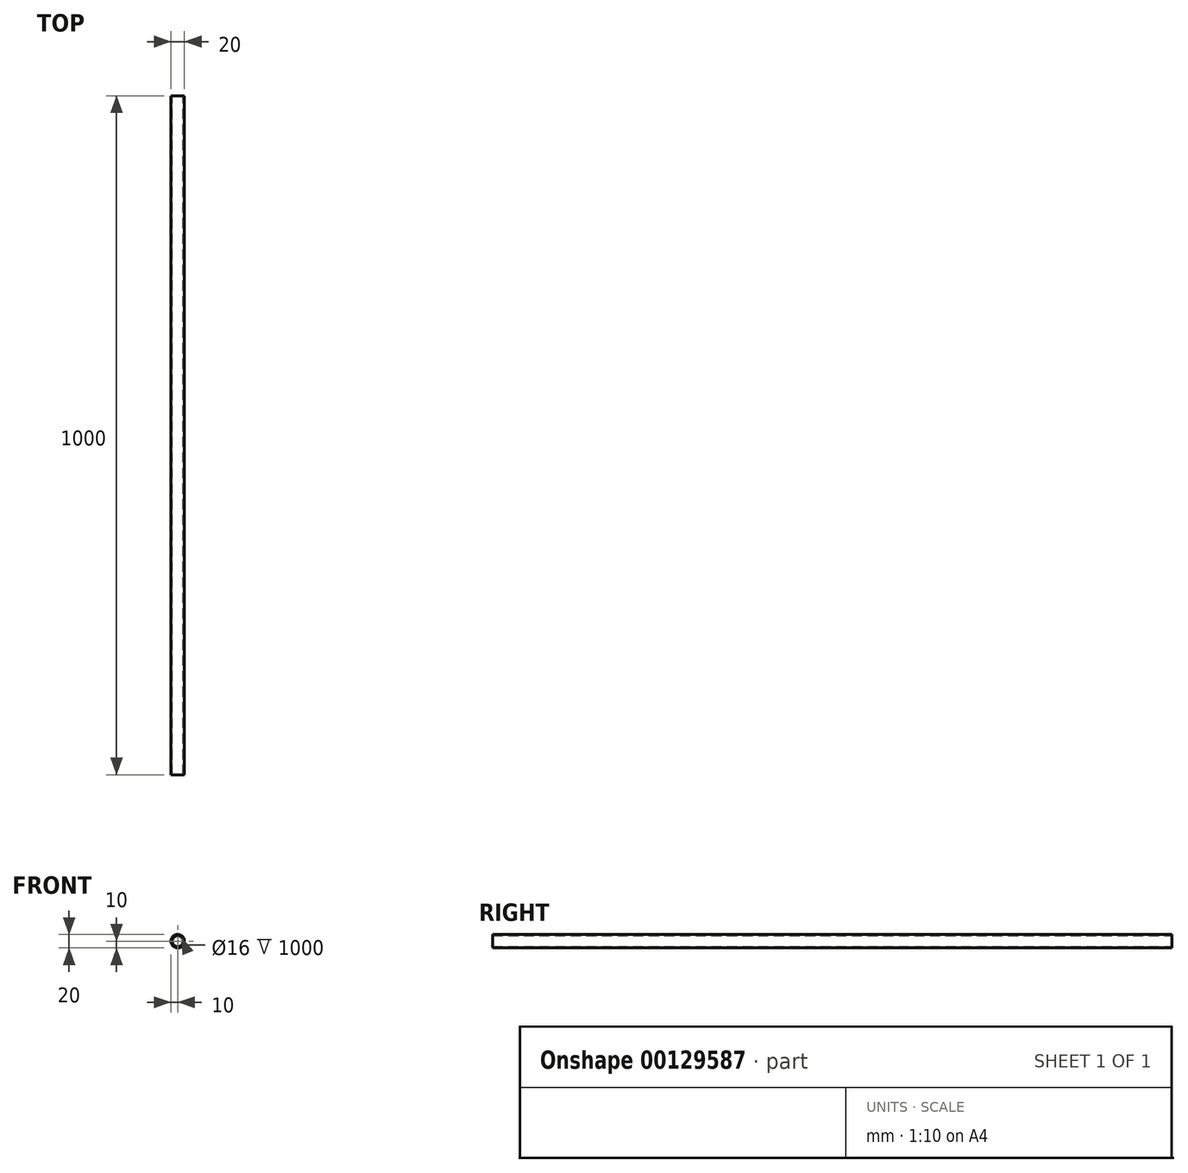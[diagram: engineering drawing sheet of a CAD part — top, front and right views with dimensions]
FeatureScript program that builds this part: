
annotation { "Feature Type Name" : "Feature", "Feature Type Description" : "" }
export const myFeature = defineFeature(function(context is Context, id is Id, definition is map)
    precondition{}
    {
        {
            var Q0;
            Q0=qCreatedBy(makeId("Front.planeOp"),FACE);
            var sketch = newSketch(context, id + "F0", { "sketchPlane" : qUnion([Q0])});
            skCircle(sketch, "E0", {"center": v(0, 0) * mm, "radius": 10 * mm});
            skCircle(sketch, "E1.0", {"center": v(0, 0) * mm, "radius": 8 * mm});
            skSolve(sketch);
        }
        {
            var Q0;
            Q0 = qSketchRegion(id + "F0", true);
            extrude(context, id + "F1", {"entities" : qUnion([Q0]), "endBound" : BoundingType.SYMMETRIC, "depth" : 1000 * mm});
        }
    });
